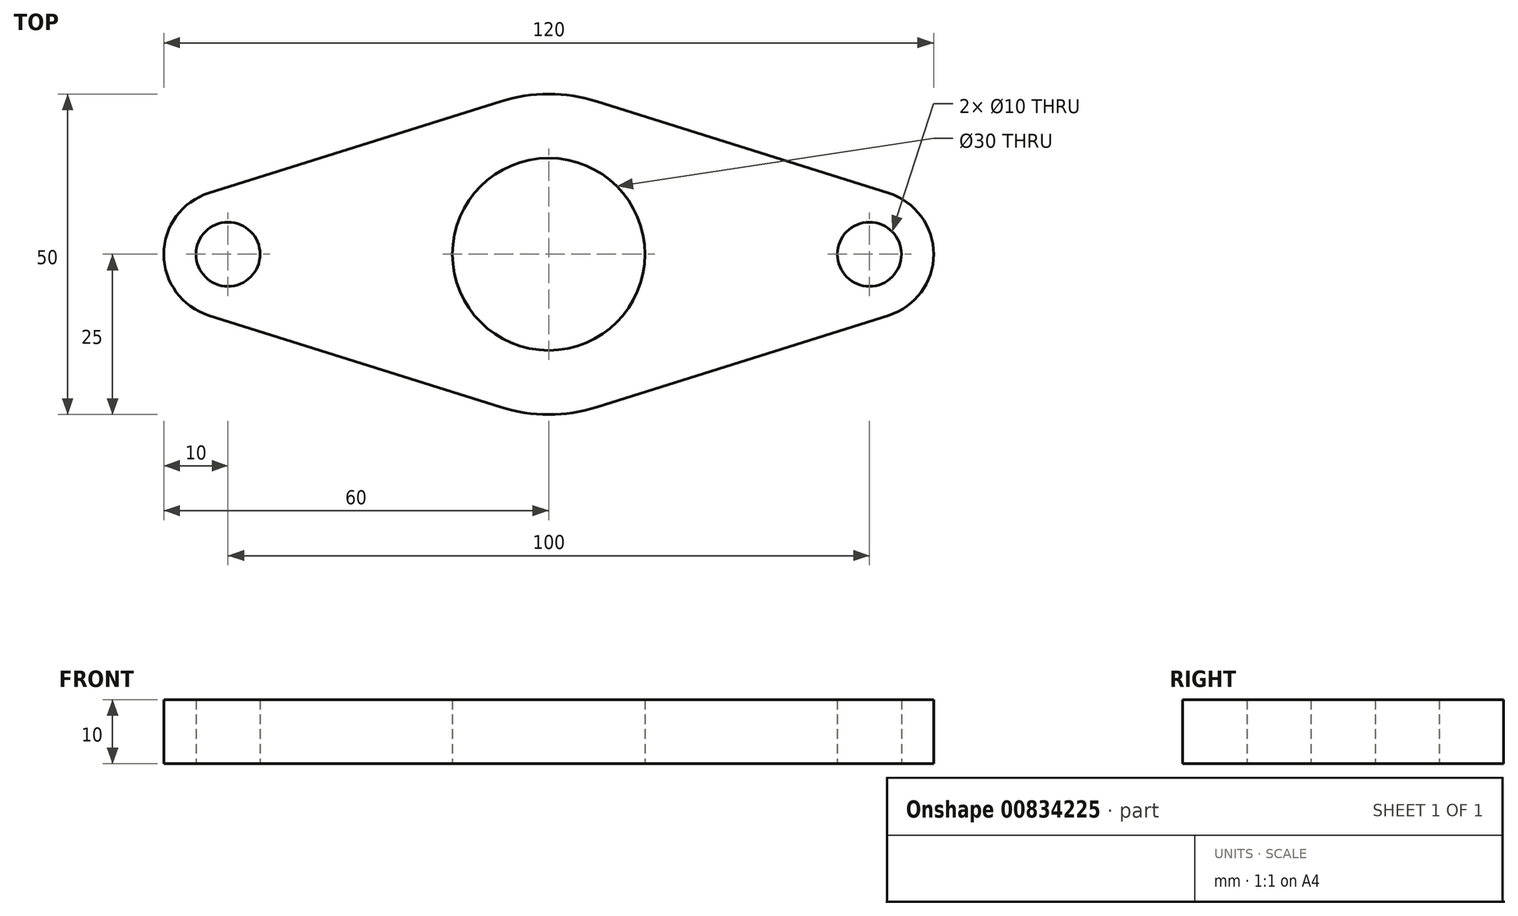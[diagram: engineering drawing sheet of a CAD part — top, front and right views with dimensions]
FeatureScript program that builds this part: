
annotation { "Feature Type Name" : "Feature", "Feature Type Description" : "" }
export const myFeature = defineFeature(function(context is Context, id is Id, definition is map)
    precondition{}
    {
        {
            var Q0;
            Q0=qCreatedBy(makeId("Top.planeOp"),FACE);
            var sketch = newSketch(context, id + "F0", { "sketchPlane" : qUnion([Q0])});
            skArc(sketch, "E0", {"start": v(-53, 9.54) * mm, "mid": v(-60, 0) * mm, "end": v(-53, -9.54) * mm});
            skArc(sketch, "E1", {"start": v(-7.5, -23.85) * mm, "mid": v(0, -25) * mm, "end": v(7.5, -23.85) * mm});
            skArc(sketch, "E2", {"start": v(53, -9.54) * mm, "mid": v(60, 0) * mm, "end": v(53, 9.54) * mm});
            skLineSegment(sketch, "E3", {"start": v(-53, 9.54) * mm, "end": v(-7.5, 23.85) * mm});
            skLineSegment(sketch, "E4", {"start": v(-53, -9.54) * mm, "end": v(-7.5, -23.85) * mm});
            skLineSegment(sketch, "E5", {"start": v(53, 9.54) * mm, "end": v(7.5, 23.85) * mm});
            skArc(sketch, "E6.trimOffspring", {"start": v(7.5, 23.85) * mm, "mid": v(0, 25) * mm, "end": v(-7.5, 23.85) * mm});
            skLineSegment(sketch, "E7", {"start": v(53, -9.54) * mm, "end": v(7.5, -23.85) * mm});
            skCircle(sketch, "E8", {"center": v(-50, 0) * mm, "radius": 5 * mm});
            skCircle(sketch, "E9", {"center": v(50, 0) * mm, "radius": 5 * mm});
            skCircle(sketch, "E10", {"center": v(0, 0) * mm, "radius": 15 * mm});
            skSolve(sketch);
        }
        {
            var Q0;
            Q0=makeQuery(id+"F0.imprint","IMPRINT",FACE,{"disambiguationData":[TD([[makeQuery(id+"F0.imprint","IMPRINT",EDGE,{"derivedFrom":sQuery(id+"F0.wireOp",EDGE,"E0")}),1.0]])]});
            extrude(context, id + "F1", {"entities" : qUnion([Q0]), "depth" : 10 * mm, "offsetDistance" : 25 * mm});
        }
    });
